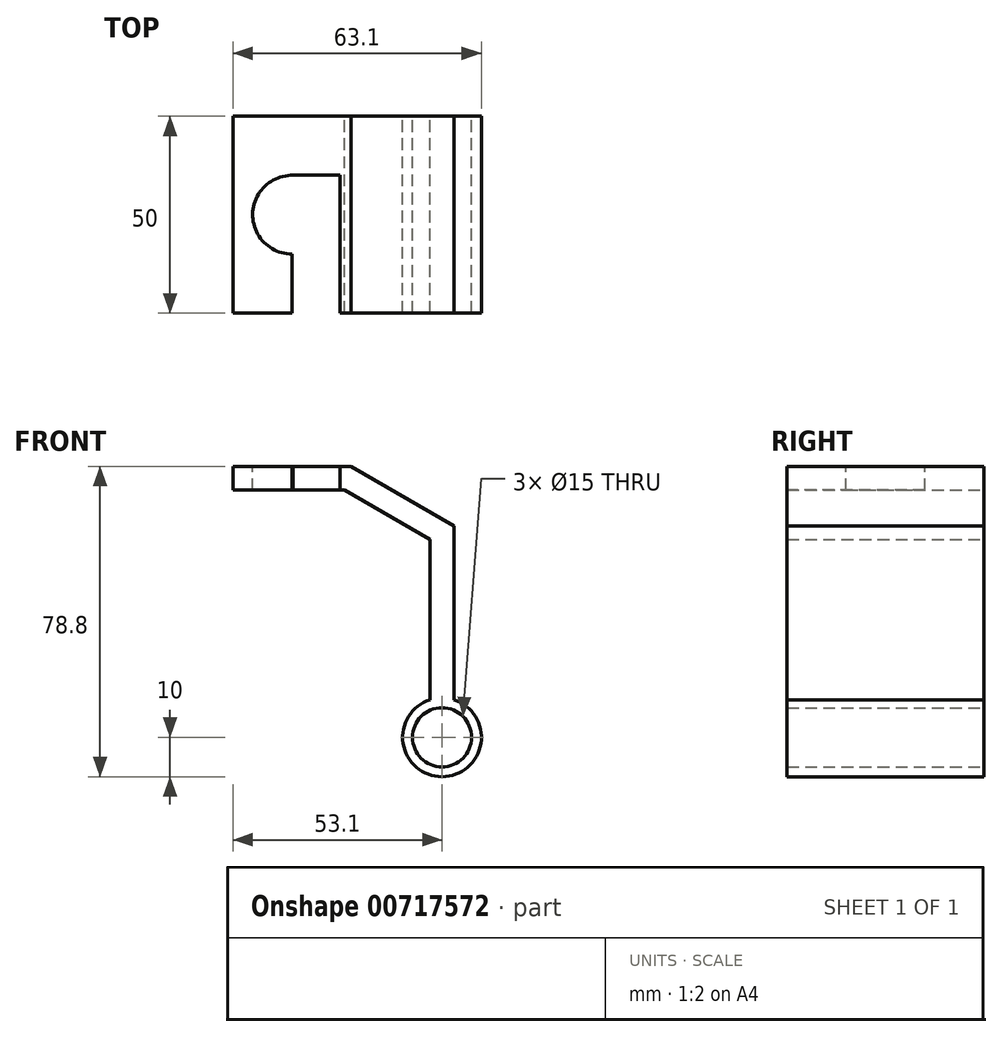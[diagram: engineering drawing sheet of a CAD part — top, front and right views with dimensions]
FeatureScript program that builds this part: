
annotation { "Feature Type Name" : "Feature", "Feature Type Description" : "" }
export const myFeature = defineFeature(function(context is Context, id is Id, definition is map)
    precondition{}
    {
        {
            var Q0;
            Q0=qCreatedBy(makeId("Front.planeOp"),FACE);
            var sketch = newSketch(context, id + "F0", { "sketchPlane" : qUnion([Q0])});
            skCircle(sketch, "E0", {"center": v(0, 0) * mm, "radius": 7.5 * mm});
            skArc(sketch, "E1", {"start": v(-3, 9.54) * mm, "mid": v(0, -10) * mm, "end": v(3, 9.54) * mm});
            skLineSegment(sketch, "E2", {"start": v(0, 0) * mm, "end": v(0, 52) * mm, "construction": true});
            skLineSegment(sketch, "E3", {"start": v(0, 52) * mm, "end": v(-23.9, 65.8) * mm, "construction": true});
            skLineSegment(sketch, "E4", {"start": v(-23.9, 65.8) * mm, "end": v(-50, 65.8) * mm, "construction": true});
            skLineSegment(sketch, "E5.0", {"start": v(-23.1, 68.8) * mm, "end": v(-53.1, 68.8) * mm});
            skLineSegment(sketch, "E5.1", {"start": v(3, 53.73) * mm, "end": v(-23.1, 68.8) * mm});
            skLineSegment(sketch, "E6.0", {"start": v(-24.7, 62.8) * mm, "end": v(-53.1, 62.8) * mm});
            skLineSegment(sketch, "E6.1", {"start": v(-3, 50.27) * mm, "end": v(-24.7, 62.8) * mm});
            skLineSegment(sketch, "E7.trimOffspring", {"start": v(3, 9.54) * mm, "end": v(3, 53.73) * mm});
            skLineSegment(sketch, "E8.trimOffspring", {"start": v(-3, 9.54) * mm, "end": v(-3, 50.27) * mm});
            skLineSegment(sketch, "E9", {"start": v(-53.1, 68.8) * mm, "end": v(-53.1, 62.8) * mm});
            skSolve(sketch);
        }
        {
            var Q0;
            Q0=makeQuery(id+"F0.imprint","IMPRINT",FACE,{"disambiguationData":[TD([[makeQuery(id+"F0.imprint","IMPRINT",EDGE,{"derivedFrom":sQuery(id+"F0.wireOp",EDGE,"E0")}),-1.0]])]});
            extrude(context, id + "F1", {"entities" : qUnion([Q0]), "depth" : 50 * mm, "offsetDistance" : 25 * mm});
        }
        {
            var Q0;
            Q0=makeQuery(id+"F1.opExtrude","SWEPT_FACE",FACE,{"disambiguationData":[OSD([sQuery(id+"F0.wireOp",EDGE,"E5.0")])]});
            var sketch = newSketch(context, id + "F2", { "sketchPlane" : qUnion([Q0])});
            skArc(sketch, "E10", {"start": v(-37.8, -15) * mm, "mid": v(-48.1, -24.85) * mm, "end": v(-38.1, -35) * mm});
            skPoint(sketch, "E10.centerSnap0", {"position": v(-53.1, -25) * mm});
            skPoint(sketch, "E10.centerSnap1", {"position": v(-38.1, 0) * mm});
            skLineSegment(sketch, "E11", {"start": v(-38.1, -35) * mm, "end": v(-38.1, -50) * mm});
            skLineSegment(sketch, "E12", {"start": v(-38.1, -50) * mm, "end": v(-25.92, -50) * mm});
            skLineSegment(sketch, "E13", {"start": v(-25.92, -50) * mm, "end": v(-25.92, -20) * mm});
            skLineSegment(sketch, "E14", {"start": v(-37.8, -15) * mm, "end": v(-25.92, -15) * mm});
            skLineSegment(sketch, "E15", {"start": v(-25.92, -15) * mm, "end": v(-25.92, -20) * mm});
            skSolve(sketch);
        }
        {
            var Q0;
            Q0=makeQuery(id+"F2.imprint","IMPRINT",FACE,{"disambiguationData":[TD([[makeQuery(id+"F2.imprint","IMPRINT",EDGE,{"derivedFrom":sQuery(id+"F2.wireOp",EDGE,"E10")}),1.0]])]});
            extrude(context, id + "F3", {"entities" : qUnion([Q0]), "operationType" : NewBodyOperationType.REMOVE, "oppositeDirection" : true, "depth" : 25 * mm, "offsetDistance" : 25 * mm});
        }
    });
